# Revit family: Plumbing_Valves_AXOR_12626000-AXOR-Starck-Porter-unit-120-120
name_source: partatom
category: Plumbing Fixtures
revit_build: Autodesk Revit 2015 (Build: 20140606_1530(x64)
units: mm (PartAtom-declared; Revit-internal decimal feet)

## types (1)
- Chrome 000
    BIMobject category = Valves
    BIMobject category code = plumbing-valves
    BIMobject main category = Plumbing
    BIMobject main category code = plumbing
    BOSUseNativeGeometries = 1
    Brand url = https://www.axor-design.com
    Default Elevation = 4' - 0"
    Design country = Germany
    EAN code = https://4011097711102
    Edition number = 1
    IFC Classification = Valve
    Installation instructions = https://pro.hansgrohe-int.com
    Manufacturer country = Germany
    Manufacturer name = AXOR
    Masterformat 2014 Code = 22 41 23
    Masterformat 2014 Description = Residential Showers
    Material main = Chrome
    NBS Reference Code = 94
    NBS Reference Description = Valves
    OmniClass Code = 23-31 11 19 11
    OmniClass Description = Thermostatically Controlled Faucet Mixing Valves
    Product Guid = ec001248-1683-47b2-b46b-24f1885d7e73
    Product SKU = 12626000
    Product data url = https://bimobject.com
    Product family = AXOR Starck
    Product group = Wall outlet
    Product name = AXOR Starck Porter unit 120/120 12626000
    Product url = https://pro.hansgrohe-int.com
    QR code = http://bimobject.com
    Technical description = https://pro.hansgrohe-int.com
    UNSPSC Code = 40141616
    Uniclass 1.4 Code = L7117
    Uniclass 1.4 Description = Valves for water supply/distribution
    Uniclass 2.0 Code = PR-94
    Uniclass 2.0 Description = Valves
    Uniclass 2015 Code = Pr_65_54
    Uniclass 2015 Name = Valve products
    Uniformat II Code = D20
    Uniformat II Description = PLUMBING

## geometry (parser evidence)
native form markers: Sweep x3
no freeform markers — native parametric forms only
